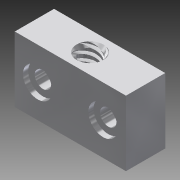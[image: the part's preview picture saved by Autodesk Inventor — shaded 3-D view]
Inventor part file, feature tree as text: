
AUTODESK INVENTOR PART (.ipt)
format: ipt  version: 2014 SP1 (Build 180222100, 222)  size: 356,864 bytes
history: native  units: in
note: dims shown in document units (in); Inventor stores cm internally (conversion verified against a paired STEP export)
features: sketch x6, extrude x5, chamfer x1, helix x1, projected_geometry x1
ambient origin geometry x8: Origin, YZ Plane, XZ Plane, XY Plane, X Axis, Y Axis, Z Axis, Center Point
bodies: Solid1 (feature_tree)
feature tree (14):
  extrude  "Extrusion1"  Depth=1.3386in
  extrude  "Extrusion2"  Depth=0.2441in
  extrude  "Extrusion3"  Depth=0.1988in
  extrude  "Extrusion4"  Depth=0.7874in
  extrude  "Extrusion5"  Depth=0.315in
  sketch  "Sketch7"  dims[d16=0.315in d17=0.1957in d18=0.0in d25=75.0deg d26=30.0deg d28=0.1614in d29=0.0433in d30=0.0787in d31=1.5748in d33=0.0787in d34=0.3937in d36=0.3937in d46=0.0394in d47=0.0787in d48=45.0deg d49=0.315in d50=1.1024in d51=0.3937in d52=0.0in d53=90.0deg d54=90.0deg d55=0.0in d56=0.0in]
  chamfer  "Chamfer1"  Distance=0.063in
  helix  "Coil2"  [1 undecoded]
  sketch  "Sketch1"  dims[d0=0.7874in d1=1.3386in]
  sketch  "Sketch2"  dims[d2=0.4724in d3=0.0in d4=0.2441in]
  sketch  "Sketch3"  dims[d5=0.4724in d6=0.0in d7=0.1988in]
  sketch  "Sketch4"  dims[d8=0.1988in d9=0.7874in]
  sketch  "Sketch5"  dims[d10=0.4724in d11=0.0in d12=0.3543in d13=0.063in d14=0.0in d15=0.315in]
  projected_geometry  "Projected Loop2"
note: 1 required parameter value undecoded (feature->parameter linkage not recoverable at this tier; creation-order binding heuristic only, values carry confidence <= 0.55)
